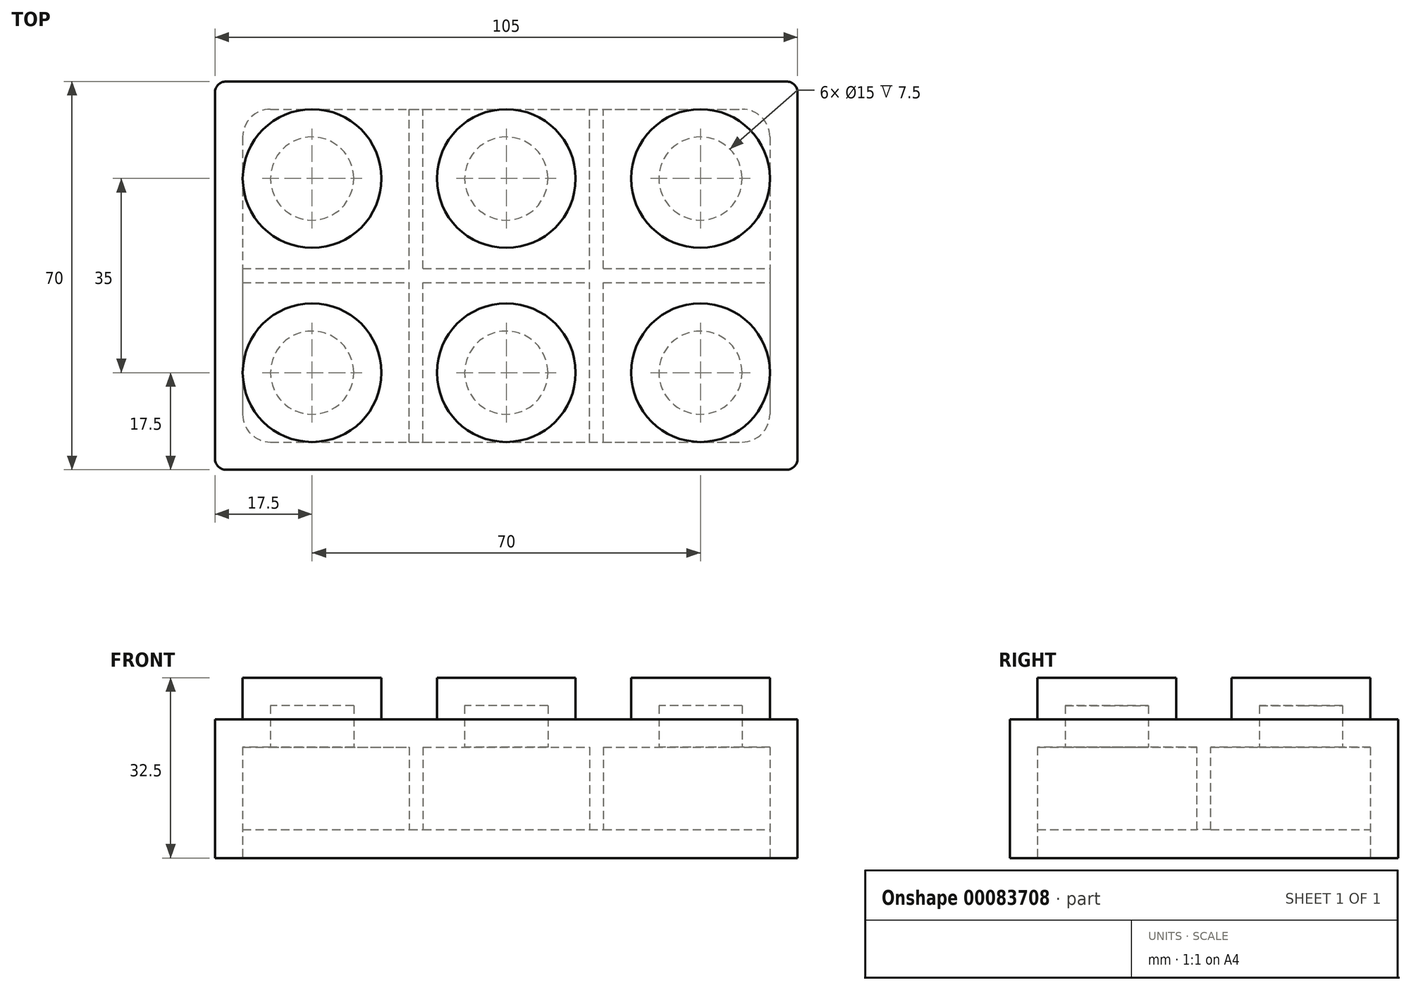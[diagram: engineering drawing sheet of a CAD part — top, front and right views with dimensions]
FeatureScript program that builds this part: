
annotation { "Feature Type Name" : "Feature", "Feature Type Description" : "" }
export const myFeature = defineFeature(function(context is Context, id is Id, definition is map)
    precondition{}
    {
        {
            var Q0;
            Q0=qCreatedBy(makeId("Top.planeOp"),FACE);
            var sketch = newSketch(context, id + "F0", { "sketchPlane" : qUnion([Q0])});
            skLineSegment(sketch, "E0.bottom", {"start": v(0, 0) * mm, "end": v(105, 0) * mm});
            skLineSegment(sketch, "E0.top", {"start": v(0, -70) * mm, "end": v(105, -70) * mm});
            skLineSegment(sketch, "E0.left", {"start": v(0, 0) * mm, "end": v(0, -70) * mm});
            skLineSegment(sketch, "E0.right", {"start": v(105, 0) * mm, "end": v(105, -70) * mm});
            skSolve(sketch);
        }
        {
            var Q0;
            Q0 = qSketchRegion(id + "F0", true);
            extrude(context, id + "F1", {"entities" : qUnion([Q0]), "depth" : 25 * mm});
        }
        {
            var Q0;
            Q0=makeQuery(id+"F1.opExtrude","CAP_FACE",FACE,{"disambiguationData":[OSD([sQuery(id+"F0.wireOp",EDGE,"E0.bottom"),sQuery(id+"F0.wireOp",EDGE,"E0.top"),sQuery(id+"F0.wireOp",EDGE,"E0.left"),sQuery(id+"F0.wireOp",EDGE,"E0.right")])],"isStart":false});
            var sketch = newSketch(context, id + "F2", { "sketchPlane" : qUnion([Q0])});
            skCircle(sketch, "E1", {"center": v(17.5, -17.5) * mm, "radius": 12.5 * mm});
            skCircle(sketch, "E2", {"center": v(52.5, -17.5) * mm, "radius": 12.5 * mm});
            skCircle(sketch, "E3", {"center": v(87.5, -17.5) * mm, "radius": 12.5 * mm});
            skCircle(sketch, "E4", {"center": v(17.5, -52.5) * mm, "radius": 12.5 * mm});
            skCircle(sketch, "E5", {"center": v(52.5, -52.5) * mm, "radius": 12.5 * mm});
            skCircle(sketch, "E6", {"center": v(87.5, -52.5) * mm, "radius": 12.5 * mm});
            skSolve(sketch);
        }
        {
            var Q0;
            Q0 = qSketchRegion(id + "F2", true);
            extrude(context, id + "F3", {"entities" : qUnion([Q0]), "operationType" : NewBodyOperationType.ADD, "depth" : 7.5 * mm});
        }
        {
            var Q0;
            Q0=makeQuery(id+"F1.opExtrude","CAP_FACE",FACE,{"disambiguationData":[OSD([sQuery(id+"F0.wireOp",EDGE,"E0.bottom"),sQuery(id+"F0.wireOp",EDGE,"E0.top"),sQuery(id+"F0.wireOp",EDGE,"E0.left"),sQuery(id+"F0.wireOp",EDGE,"E0.right")])],"isStart":true});
            shell(context, id + "F4", {"entities" : qUnion([Q0]), "thickness" : 5 * mm});
        }
        {
            var Q0;
            Q0=qCreatedBy(makeId("Top.planeOp"),FACE);
            cPlane(context, id + "F5", {"entities" : qUnion([Q0]), "cplaneType" : CPlaneType.OFFSET, "offset" : 5.1 * mm, "width" : 150 * mm, "height" : 150 * mm});
        }
        {
            var Q0;
            Q0=qCreatedBy(id+"F5.planeOp",FACE);
            var sketch = newSketch(context, id + "F6", { "sketchPlane" : qUnion([Q0])});
            skLineSegment(sketch, "E7.0", {"start": v(5, -33.75) * mm, "end": v(5, -36.25) * mm});
            skLineSegment(sketch, "E8.0", {"start": v(100, -33.75) * mm, "end": v(100, -36.25) * mm});
            skLineSegment(sketch, "E9", {"start": v(5, -36.25) * mm, "end": v(100, -36.25) * mm});
            skLineSegment(sketch, "E10", {"start": v(5, -33.75) * mm, "end": v(100, -33.75) * mm});
            skPoint(sketch, "E11.orphan", {"position": v(5, -65) * mm});
            skPoint(sketch, "E12.orphan", {"position": v(5, -5) * mm});
            skPoint(sketch, "E13.orphan", {"position": v(100, -5) * mm});
            skPoint(sketch, "E14.orphan", {"position": v(100, -65) * mm});
            skSolve(sketch);
        }
        {
            var Q0;
            Q0 = qSketchRegion(id + "F6", true);
            extrude(context, id + "F7", {"entities" : qUnion([Q0]), "operationType" : NewBodyOperationType.ADD, "endBound" : BoundingType.UP_TO_NEXT, "depth" : 25 * mm});
        }
        {
            var Q0;
            Q0=qCreatedBy(id+"F5.planeOp",FACE);
            var sketch = newSketch(context, id + "F8", { "sketchPlane" : qUnion([Q0])});
            skLineSegment(sketch, "E15.0", {"start": v(35, -65) * mm, "end": v(37.5, -65) * mm});
            skLineSegment(sketch, "E16.0", {"start": v(35, -5) * mm, "end": v(37.5, -5) * mm});
            skLineSegment(sketch, "E17", {"start": v(35, -65) * mm, "end": v(35, -5) * mm});
            skLineSegment(sketch, "E18", {"start": v(37.5, -65) * mm, "end": v(37.5, -5) * mm});
            skPoint(sketch, "E19.orphan", {"position": v(5, -65) * mm});
            skPoint(sketch, "E20.orphan", {"position": v(5, -5) * mm});
            skPoint(sketch, "E21.orphan", {"position": v(100, -5) * mm});
            skPoint(sketch, "E22.orphan", {"position": v(100, -65) * mm});
            skLineSegment(sketch, "E23", {"start": v(67.5, -65) * mm, "end": v(67.5, -5) * mm});
            skLineSegment(sketch, "E24", {"start": v(70, -65) * mm, "end": v(70, -5) * mm});
            skLineSegment(sketch, "E25.trimOffspring", {"start": v(67.5, -65) * mm, "end": v(70, -65) * mm});
            skLineSegment(sketch, "E26.trimOffspring", {"start": v(67.5, -5) * mm, "end": v(70, -5) * mm});
            skSolve(sketch);
        }
        {
            var Q0;
            Q0 = qSketchRegion(id + "F8", true);
            var Q1;
            {var subQ0=sQuery(id+"F0.wireOp",EDGE,"E0.right");var subQ3=sQuery(id+"F0.wireOp",EDGE,"E0.left");var subQ4=sQuery(id+"F0.wireOp",EDGE,"E0.top");Q1=makeQuery(id+"F7.boolean.opBoolean","SPLIT",FACE,{"disambiguationData":[TD([makeQuery(id+"F4.opShell","OFFSET_FACE",FACE,{"disambiguationData":[OSD([subQ4])]})])],"derivedFrom":makeQuery(id+"F4.opShell","OFFSET_FACE",FACE,{"disambiguationData":[OSD([sQuery(id+"F0.wireOp",EDGE,"E0.bottom"),subQ4,subQ3,subQ0])]})});}
            extrude(context, id + "F9", {"entities" : qUnion([Q0]), "operationType" : NewBodyOperationType.ADD, "endBound" : BoundingType.UP_TO_SURFACE, "endBoundEntityFace" : qUnion([Q1]), "depth" : 25 * mm});
        }
        {
            var Q0;
            Q0=makeQuery(id+"F4.opShell","OFFSET_EDGE",EDGE,{"disambiguationData":[OSD([sQuery(id+"F0.wireOp",EDGE,"E0.top"),sQuery(id+"F0.wireOp",EDGE,"E0.left")])]});
            var Q1;
            Q1=makeQuery(id+"F4.opShell","OFFSET_EDGE",EDGE,{"disambiguationData":[OSD([sQuery(id+"F0.wireOp",EDGE,"E0.bottom"),sQuery(id+"F0.wireOp",EDGE,"E0.left")])]});
            var Q2;
            Q2=makeQuery(id+"F4.opShell","OFFSET_EDGE",EDGE,{"disambiguationData":[OSD([sQuery(id+"F0.wireOp",EDGE,"E0.top"),sQuery(id+"F0.wireOp",EDGE,"E0.right")])]});
            var Q3;
            Q3=makeQuery(id+"F4.opShell","OFFSET_EDGE",EDGE,{"disambiguationData":[OSD([sQuery(id+"F0.wireOp",EDGE,"E0.bottom"),sQuery(id+"F0.wireOp",EDGE,"E0.right")])]});
            fillet(context, id + "F10", {"entities" : qUnion([Q0, Q1, Q2, Q3]), "radius" : 5 * mm, "tangentPropagation" : true, "allowEdgeOverflow" : false});
        }
        {
            var Q0;
            Q0=makeQuery(id+"F1.opExtrude","SWEPT_EDGE",EDGE,{"disambiguationData":[OSD([sQuery(id+"F0.wireOp",EDGE,"E0.top"),sQuery(id+"F0.wireOp",EDGE,"E0.right")])]});
            var Q1;
            Q1=makeQuery(id+"F1.opExtrude","SWEPT_EDGE",EDGE,{"disambiguationData":[OSD([sQuery(id+"F0.wireOp",EDGE,"E0.top"),sQuery(id+"F0.wireOp",EDGE,"E0.left")])]});
            var Q2;
            Q2=makeQuery(id+"F1.opExtrude","SWEPT_EDGE",EDGE,{"disambiguationData":[OSD([sQuery(id+"F0.wireOp",EDGE,"E0.bottom"),sQuery(id+"F0.wireOp",EDGE,"E0.left")])]});
            var Q3;
            Q3=makeQuery(id+"F1.opExtrude","SWEPT_EDGE",EDGE,{"disambiguationData":[OSD([sQuery(id+"F0.wireOp",EDGE,"E0.bottom"),sQuery(id+"F0.wireOp",EDGE,"E0.right")])]});
            fillet(context, id + "F11", {"entities" : qUnion([Q0, Q1, Q2, Q3]), "radius" : 2 * mm, "tangentPropagation" : true, "allowEdgeOverflow" : false});
        }
    });
